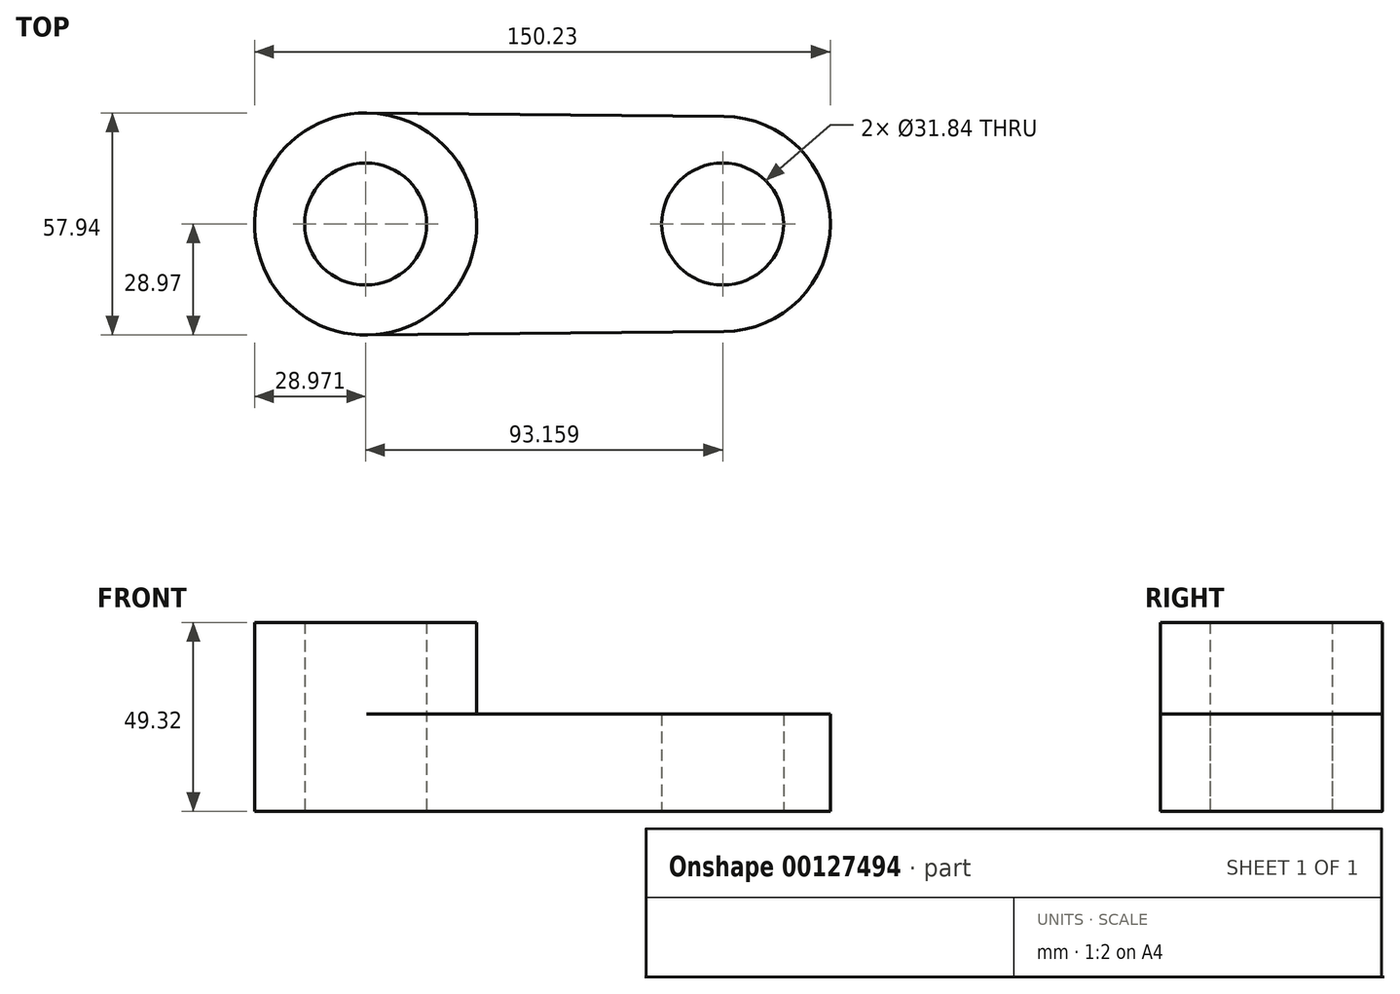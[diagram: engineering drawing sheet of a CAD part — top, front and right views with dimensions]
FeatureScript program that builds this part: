
annotation { "Feature Type Name" : "Feature", "Feature Type Description" : "" }
export const myFeature = defineFeature(function(context is Context, id is Id, definition is map)
    precondition{}
    {
        {
            var Q0;
            Q0=qCreatedBy(makeId("Top.planeOp"),FACE);
            var sketch = newSketch(context, id + "F0", { "sketchPlane" : qUnion([Q0])});
            skCircle(sketch, "E0", {"center": v(-46.58, 0) * mm, "radius": 15.92 * mm});
            skCircle(sketch, "E1", {"center": v(46.58, 0) * mm, "radius": 15.92 * mm});
            skArc(sketch, "E2", {"start": v(-46.3, 28.97) * mm, "mid": v(-75.55, 0) * mm, "end": v(-46.3, -28.97) * mm});
            skArc(sketch, "E3", {"start": v(46.84, -28.1) * mm, "mid": v(74.68, 0) * mm, "end": v(46.84, 28.1) * mm});
            skLineSegment(sketch, "E4", {"start": v(-46.3, 28.97) * mm, "end": v(46.84, 28.1) * mm});
            skLineSegment(sketch, "E5", {"start": v(46.84, -28.1) * mm, "end": v(-46.3, -28.97) * mm});
            skArc(sketch, "E6", {"start": v(-46.3, -28.97) * mm, "mid": v(-17.6, 0) * mm, "end": v(-46.3, 28.97) * mm});
            skSolve(sketch);
        }
        {
            var Q0;
            Q0=makeQuery(id+"F0.imprint","IMPRINT",FACE,{"disambiguationData":[TD([[makeQuery(id+"F0.imprint","IMPRINT",EDGE,{"derivedFrom":sQuery(id+"F0.wireOp",EDGE,"E0")}),-1.0]])]});
            var Q1;
            Q1=makeQuery(id+"F0.imprint","IMPRINT",FACE,{"disambiguationData":[TD([[makeQuery(id+"F0.imprint","IMPRINT",EDGE,{"derivedFrom":sQuery(id+"F0.wireOp",EDGE,"E1")}),-1.0]])]});
            extrude(context, id + "F1", {"entities" : qUnion([Q0, Q1]), "depth" : 25.4 * mm});
        }
        {
            var Q0;
            Q0=makeQuery(id+"F0.imprint","IMPRINT",FACE,{"disambiguationData":[TD([[makeQuery(id+"F0.imprint","IMPRINT",EDGE,{"derivedFrom":sQuery(id+"F0.wireOp",EDGE,"E0")}),-1.0]])]});
            extrude(context, id + "F2", {"entities" : qUnion([Q0]), "operationType" : NewBodyOperationType.ADD, "depth" : 49.32 * mm});
        }
    });
